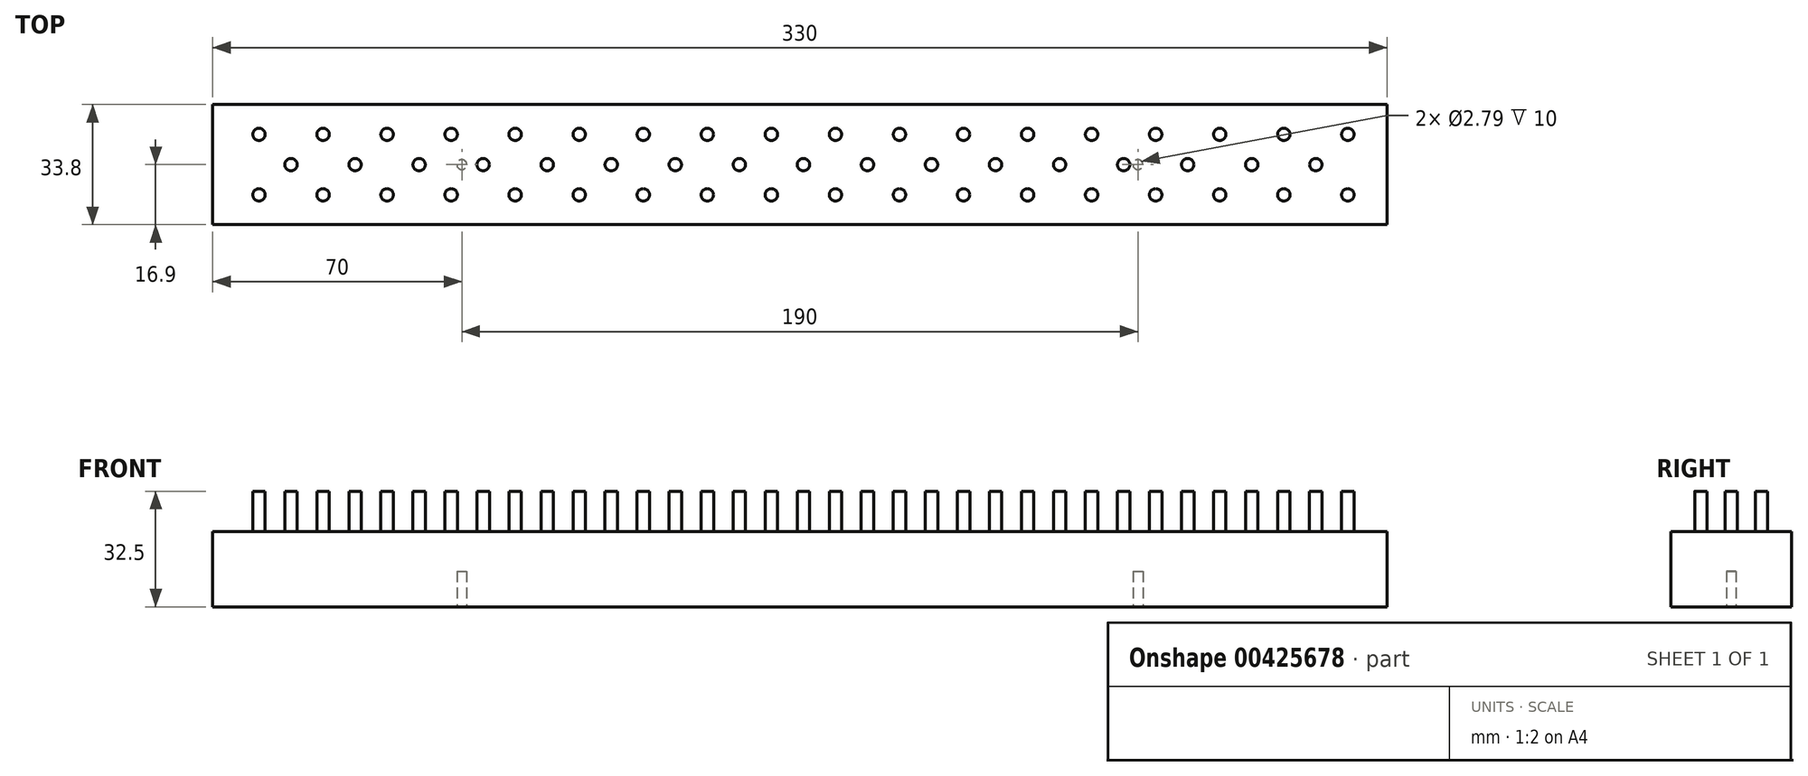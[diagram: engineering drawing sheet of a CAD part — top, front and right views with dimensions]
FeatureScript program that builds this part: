
annotation { "Feature Type Name" : "Feature", "Feature Type Description" : "" }
export const myFeature = defineFeature(function(context is Context, id is Id, definition is map)
    precondition{}
    {
        {
            var Q0;
            Q0=qCreatedBy(makeId("Top.planeOp"),FACE);
            var sketch = newSketch(context, id + "F0", { "sketchPlane" : qUnion([Q0])});
            skLineSegment(sketch, "E0.bottom", {"start": v(-70, 16.9) * mm, "end": v(260, 16.9) * mm});
            skLineSegment(sketch, "E0.top", {"start": v(-70, -16.9) * mm, "end": v(260, -16.9) * mm});
            skLineSegment(sketch, "E0.left", {"start": v(-70, 16.9) * mm, "end": v(-70, -16.9) * mm});
            skLineSegment(sketch, "E0.right", {"start": v(260, 16.9) * mm, "end": v(260, -16.9) * mm});
            skSolve(sketch);
        }
        {
            var Q0;
            Q0 = qSketchRegion(id + "F0", true);
            extrude(context, id + "F1", {"entities" : qUnion([Q0]), "depth" : 21.2 * mm, "offsetDistance" : 25 * mm});
        }
        {
            var Q0;
            Q0=makeQuery(id+"F1.opExtrude","CAP_FACE",FACE,{"disambiguationData":[OSD([sQuery(id+"F0.wireOp",EDGE,"E0.bottom"),sQuery(id+"F0.wireOp",EDGE,"E0.top"),sQuery(id+"F0.wireOp",EDGE,"E0.left"),sQuery(id+"F0.wireOp",EDGE,"E0.right")])],"isStart":true});
            var sketch = newSketch(context, id + "F2", { "sketchPlane" : qUnion([Q0])});
            skCircle(sketch, "E1", {"center": v(0, 0) * mm, "radius": 1.4 * mm});
            skCircle(sketch, "E2", {"center": v(190, 0) * mm, "radius": 1.4 * mm});
            skSolve(sketch);
        }
        {
            var Q0;
            Q0 = qSketchRegion(id + "F2", true);
            extrude(context, id + "F3", {"entities" : qUnion([Q0]), "operationType" : NewBodyOperationType.REMOVE, "oppositeDirection" : true, "depth" : 10 * mm, "offsetDistance" : 25 * mm});
        }
        {
            var Q0;
            Q0=makeQuery(id+"F1.opExtrude","CAP_FACE",FACE,{"disambiguationData":[OSD([sQuery(id+"F0.wireOp",EDGE,"E0.bottom"),sQuery(id+"F0.wireOp",EDGE,"E0.top"),sQuery(id+"F0.wireOp",EDGE,"E0.left"),sQuery(id+"F0.wireOp",EDGE,"E0.right")])],"isStart":false});
            var sketch = newSketch(context, id + "F4", { "sketchPlane" : qUnion([Q0])});
            skCircle(sketch, "E3", {"center": v(-57, 8.5) * mm, "radius": 1.75 * mm});
            skCircle(sketch, "E4", {"center": v(-57, -8.5) * mm, "radius": 1.75 * mm});
            skCircle(sketch, "E5", {"center": v(-48, 0) * mm, "radius": 1.75 * mm});
            skCircle(sketch, "E6.1.0.0", {"center": v(-39, 8.5) * mm, "radius": 1.75 * mm});
            skCircle(sketch, "E6.1.0.1", {"center": v(-39, -8.5) * mm, "radius": 1.75 * mm});
            skCircle(sketch, "E6.1.0.2", {"center": v(-30, 0) * mm, "radius": 1.75 * mm});
            skCircle(sketch, "E6.2.0.0", {"center": v(-21, 8.5) * mm, "radius": 1.75 * mm});
            skCircle(sketch, "E6.2.0.1", {"center": v(-21, -8.5) * mm, "radius": 1.75 * mm});
            skCircle(sketch, "E6.2.0.2", {"center": v(-12, 0) * mm, "radius": 1.75 * mm});
            skCircle(sketch, "E6.3.0.0", {"center": v(-3, 8.5) * mm, "radius": 1.75 * mm});
            skCircle(sketch, "E6.3.0.1", {"center": v(-3, -8.5) * mm, "radius": 1.75 * mm});
            skCircle(sketch, "E6.3.0.2", {"center": v(6, 0) * mm, "radius": 1.75 * mm});
            skCircle(sketch, "E6.4.0.0", {"center": v(15, 8.5) * mm, "radius": 1.75 * mm});
            skCircle(sketch, "E6.4.0.1", {"center": v(15, -8.5) * mm, "radius": 1.75 * mm});
            skCircle(sketch, "E6.4.0.2", {"center": v(24, 0) * mm, "radius": 1.75 * mm});
            skCircle(sketch, "E6.5.0.0", {"center": v(33, 8.5) * mm, "radius": 1.75 * mm});
            skCircle(sketch, "E6.5.0.1", {"center": v(33, -8.5) * mm, "radius": 1.75 * mm});
            skCircle(sketch, "E6.5.0.2", {"center": v(42, 0) * mm, "radius": 1.75 * mm});
            skCircle(sketch, "E6.6.0.0", {"center": v(51, 8.5) * mm, "radius": 1.75 * mm});
            skCircle(sketch, "E6.6.0.1", {"center": v(51, -8.5) * mm, "radius": 1.75 * mm});
            skCircle(sketch, "E6.6.0.2", {"center": v(60, 0) * mm, "radius": 1.75 * mm});
            skCircle(sketch, "E6.7.0.0", {"center": v(69, 8.5) * mm, "radius": 1.75 * mm});
            skCircle(sketch, "E6.7.0.1", {"center": v(69, -8.5) * mm, "radius": 1.75 * mm});
            skCircle(sketch, "E6.7.0.2", {"center": v(78, 0) * mm, "radius": 1.75 * mm});
            skCircle(sketch, "E6.8.0.0", {"center": v(87, 8.5) * mm, "radius": 1.75 * mm});
            skCircle(sketch, "E6.8.0.1", {"center": v(87, -8.5) * mm, "radius": 1.75 * mm});
            skCircle(sketch, "E6.8.0.2", {"center": v(96, 0) * mm, "radius": 1.75 * mm});
            skCircle(sketch, "E6.9.0.0", {"center": v(105, 8.5) * mm, "radius": 1.75 * mm});
            skCircle(sketch, "E6.9.0.1", {"center": v(105, -8.5) * mm, "radius": 1.75 * mm});
            skCircle(sketch, "E6.9.0.2", {"center": v(114, 0) * mm, "radius": 1.75 * mm});
            skCircle(sketch, "E6.10.0.0", {"center": v(123, 8.5) * mm, "radius": 1.75 * mm});
            skCircle(sketch, "E6.10.0.1", {"center": v(123, -8.5) * mm, "radius": 1.75 * mm});
            skCircle(sketch, "E6.10.0.2", {"center": v(132, 0) * mm, "radius": 1.75 * mm});
            skCircle(sketch, "E6.11.0.0", {"center": v(141, 8.5) * mm, "radius": 1.75 * mm});
            skCircle(sketch, "E6.11.0.1", {"center": v(141, -8.5) * mm, "radius": 1.75 * mm});
            skCircle(sketch, "E6.11.0.2", {"center": v(150, 0) * mm, "radius": 1.75 * mm});
            skCircle(sketch, "E6.12.0.0", {"center": v(159, 8.5) * mm, "radius": 1.75 * mm});
            skCircle(sketch, "E6.12.0.1", {"center": v(159, -8.5) * mm, "radius": 1.75 * mm});
            skCircle(sketch, "E6.12.0.2", {"center": v(168, 0) * mm, "radius": 1.75 * mm});
            skCircle(sketch, "E6.13.0.0", {"center": v(177, 8.5) * mm, "radius": 1.75 * mm});
            skCircle(sketch, "E6.13.0.1", {"center": v(177, -8.5) * mm, "radius": 1.75 * mm});
            skCircle(sketch, "E6.13.0.2", {"center": v(186, 0) * mm, "radius": 1.75 * mm});
            skCircle(sketch, "E6.14.0.0", {"center": v(195, 8.5) * mm, "radius": 1.75 * mm});
            skCircle(sketch, "E6.14.0.1", {"center": v(195, -8.5) * mm, "radius": 1.75 * mm});
            skCircle(sketch, "E6.14.0.2", {"center": v(204, 0) * mm, "radius": 1.75 * mm});
            skCircle(sketch, "E6.15.0.0", {"center": v(213, 8.5) * mm, "radius": 1.75 * mm});
            skCircle(sketch, "E6.15.0.1", {"center": v(213, -8.5) * mm, "radius": 1.75 * mm});
            skCircle(sketch, "E6.15.0.2", {"center": v(222, 0) * mm, "radius": 1.75 * mm});
            skCircle(sketch, "E6.16.0.0", {"center": v(231, 8.5) * mm, "radius": 1.75 * mm});
            skCircle(sketch, "E6.16.0.1", {"center": v(231, -8.5) * mm, "radius": 1.75 * mm});
            skCircle(sketch, "E6.16.0.2", {"center": v(240, 0) * mm, "radius": 1.75 * mm});
            skCircle(sketch, "E6.17.0.0", {"center": v(249, 8.5) * mm, "radius": 1.75 * mm});
            skCircle(sketch, "E6.17.0.1", {"center": v(249, -8.5) * mm, "radius": 1.75 * mm});
            skLineSegment(sketch, "E6.direction1", {"start": v(-57, 8.5) * mm, "end": v(-39, 8.5) * mm, "construction": true});
            skSolve(sketch);
        }
        {
            var Q0;
            Q0 = qSketchRegion(id + "F4", true);
            extrude(context, id + "F5", {"entities" : qUnion([Q0]), "operationType" : NewBodyOperationType.ADD, "depth" : 11.3 * mm, "offsetDistance" : 25 * mm});
        }
    });
